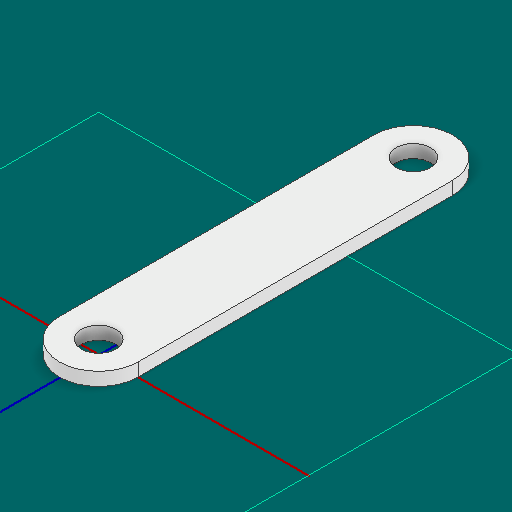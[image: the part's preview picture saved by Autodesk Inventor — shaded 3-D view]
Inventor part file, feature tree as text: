
AUTODESK INVENTOR PART (.ipt)
format: ipt  version: 2025 (Build 290162000, 162)  size: 103,936 bytes
history: native  units: in
note: dims shown in document units (in); Inventor stores cm internally (conversion verified against a paired STEP export)
features: extrude x1, sketch x1
ambient origin geometry x8: Origin, YZ Plane, XZ Plane, XY Plane, X Axis, Y Axis, Z Axis, Center Point
bodies: Solid1 (feature_tree)
feature tree (2):
  extrude  "Extrusion1"  Depth=1.5in
  sketch  "Sketch2"  dims[d0=0.165in d1=0.105in d2=0.165in d3=0.0625in d4=0.0in d5=1.5in]
